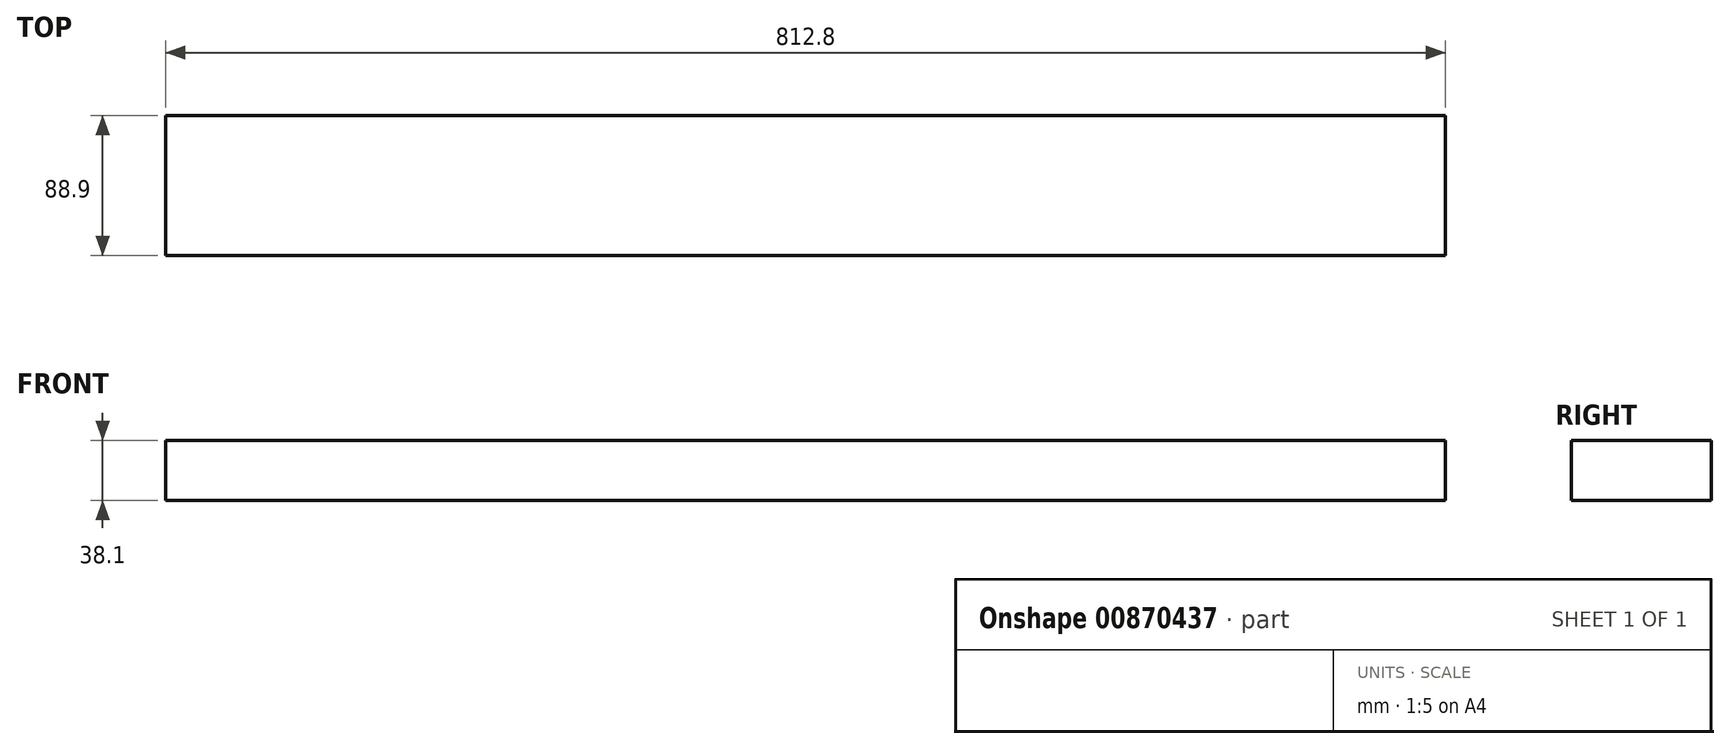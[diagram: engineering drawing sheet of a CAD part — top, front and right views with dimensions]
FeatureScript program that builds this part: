
annotation { "Feature Type Name" : "Feature", "Feature Type Description" : "" }
export const myFeature = defineFeature(function(context is Context, id is Id, definition is map)
    precondition{}
    {
        {
            var Q0;
            Q0=qCreatedBy(makeId("Right.planeOp"),FACE);
            var sketch = newSketch(context, id + "F0", { "sketchPlane" : qUnion([Q0])});
            skLineSegment(sketch, "E0.bottom", {"start": v(46.26, 19.05) * mm, "end": v(-42.64, 19.05) * mm});
            skLineSegment(sketch, "E0.top", {"start": v(46.26, -19.05) * mm, "end": v(-42.64, -19.05) * mm});
            skLineSegment(sketch, "E0.left", {"start": v(46.26, 19.05) * mm, "end": v(46.26, -19.05) * mm});
            skLineSegment(sketch, "E0.right", {"start": v(-42.64, 19.05) * mm, "end": v(-42.64, -19.05) * mm});
            skPoint(sketch, "E0.middle", {"position": v(1.8, 0) * mm});
            skSolve(sketch);
        }
        {
            var Q0;
            Q0=makeQuery(id+"F0.imprint","IMPRINT",FACE,{"disambiguationData":[TD([[makeQuery(id+"F0.imprint","IMPRINT",EDGE,{"derivedFrom":sQuery(id+"F0.wireOp",EDGE,"E0.bottom")}),1.0]])]});
            extrude(context, id + "F1", {"entities" : qUnion([Q0]), "depth" : 812.8 * mm, "offsetDistance" : 25.4 * mm});
        }
    });
